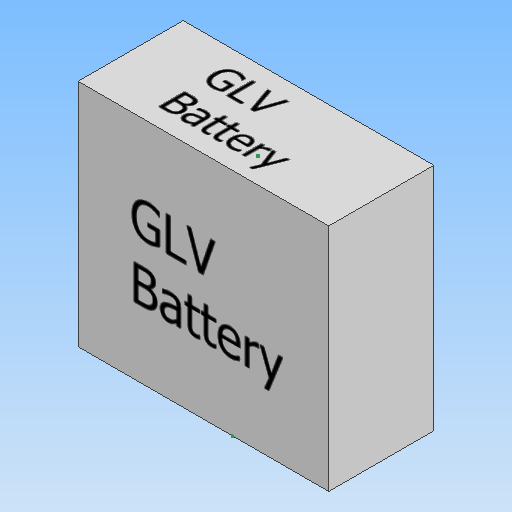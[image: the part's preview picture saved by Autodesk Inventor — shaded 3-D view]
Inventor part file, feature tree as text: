
AUTODESK INVENTOR PART (.ipt)
format: ipt  version: 2021 (Build 250183000, 183)  size: 101,888 bytes
history: native  units: in
note: dims shown in document units (in); Inventor stores cm internally (conversion verified against a paired STEP export)
features: sketch x3, extrude x1
ambient origin geometry x8: Origin, YZ Plane, XZ Plane, XY Plane, X Axis, Y Axis, Z Axis, Center Point
bodies: Solid1 (feature_tree)
feature tree (4):
  extrude  "Extrusion1"  Depth=7.13in
  sketch  "Sketch2"  dims[d3=6.54in]
  sketch  "Sketch3"  dims[d4=0.0in]
  sketch  "Sketch1"  dims[d1=2.99in d2=7.13in]
